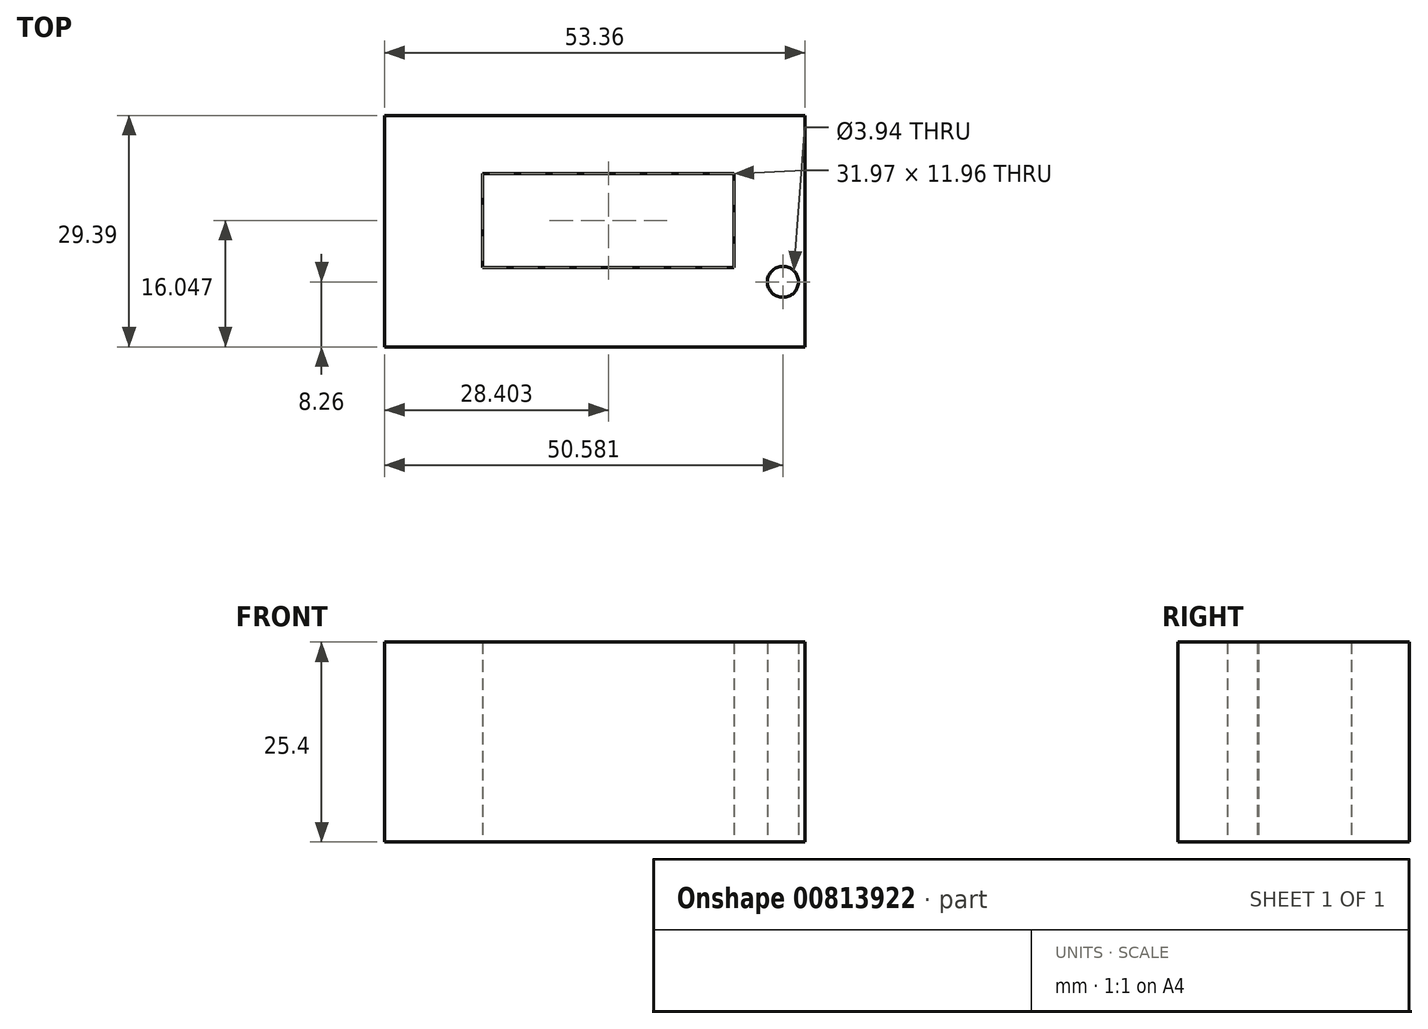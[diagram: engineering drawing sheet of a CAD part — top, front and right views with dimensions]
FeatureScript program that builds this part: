
annotation { "Feature Type Name" : "Feature", "Feature Type Description" : "" }
export const myFeature = defineFeature(function(context is Context, id is Id, definition is map)
    precondition{}
    {
        {
            var Q0;
            Q0=qCreatedBy(makeId("Top.planeOp"),FACE);
            var sketch = newSketch(context, id + "F0", { "sketchPlane" : qUnion([Q0])});
            skLineSegment(sketch, "E0.bottom", {"start": v(0, 0) * mm, "end": v(53.36, 0) * mm});
            skLineSegment(sketch, "E0.top", {"start": v(0, 29.39) * mm, "end": v(53.36, 29.39) * mm});
            skLineSegment(sketch, "E0.left", {"start": v(0, 0) * mm, "end": v(0, 29.39) * mm});
            skLineSegment(sketch, "E0.right", {"start": v(53.36, 0) * mm, "end": v(53.36, 29.39) * mm});
            skLineSegment(sketch, "E1.bottom", {"start": v(12.42, 10.07) * mm, "end": v(44.39, 10.07) * mm});
            skLineSegment(sketch, "E1.top", {"start": v(12.42, 22.03) * mm, "end": v(44.39, 22.03) * mm});
            skLineSegment(sketch, "E1.left", {"start": v(12.42, 10.07) * mm, "end": v(12.42, 22.03) * mm});
            skLineSegment(sketch, "E1.right", {"start": v(44.39, 10.07) * mm, "end": v(44.39, 22.03) * mm});
            skCircle(sketch, "E2", {"center": v(50.58, 8.26) * mm, "radius": 1.97 * mm});
            skSolve(sketch);
        }
        {
            var Q0;
            Q0=makeQuery(id+"F0.imprint","IMPRINT",FACE,{"disambiguationData":[TD([[makeQuery(id+"F0.imprint","IMPRINT",EDGE,{"derivedFrom":sQuery(id+"F0.wireOp",EDGE,"E0.bottom")}),1.0]])]});
            extrude(context, id + "F1", {"entities" : qUnion([Q0]), "depth" : 25.4 * mm, "offsetDistance" : 25.4 * mm});
        }
    });
